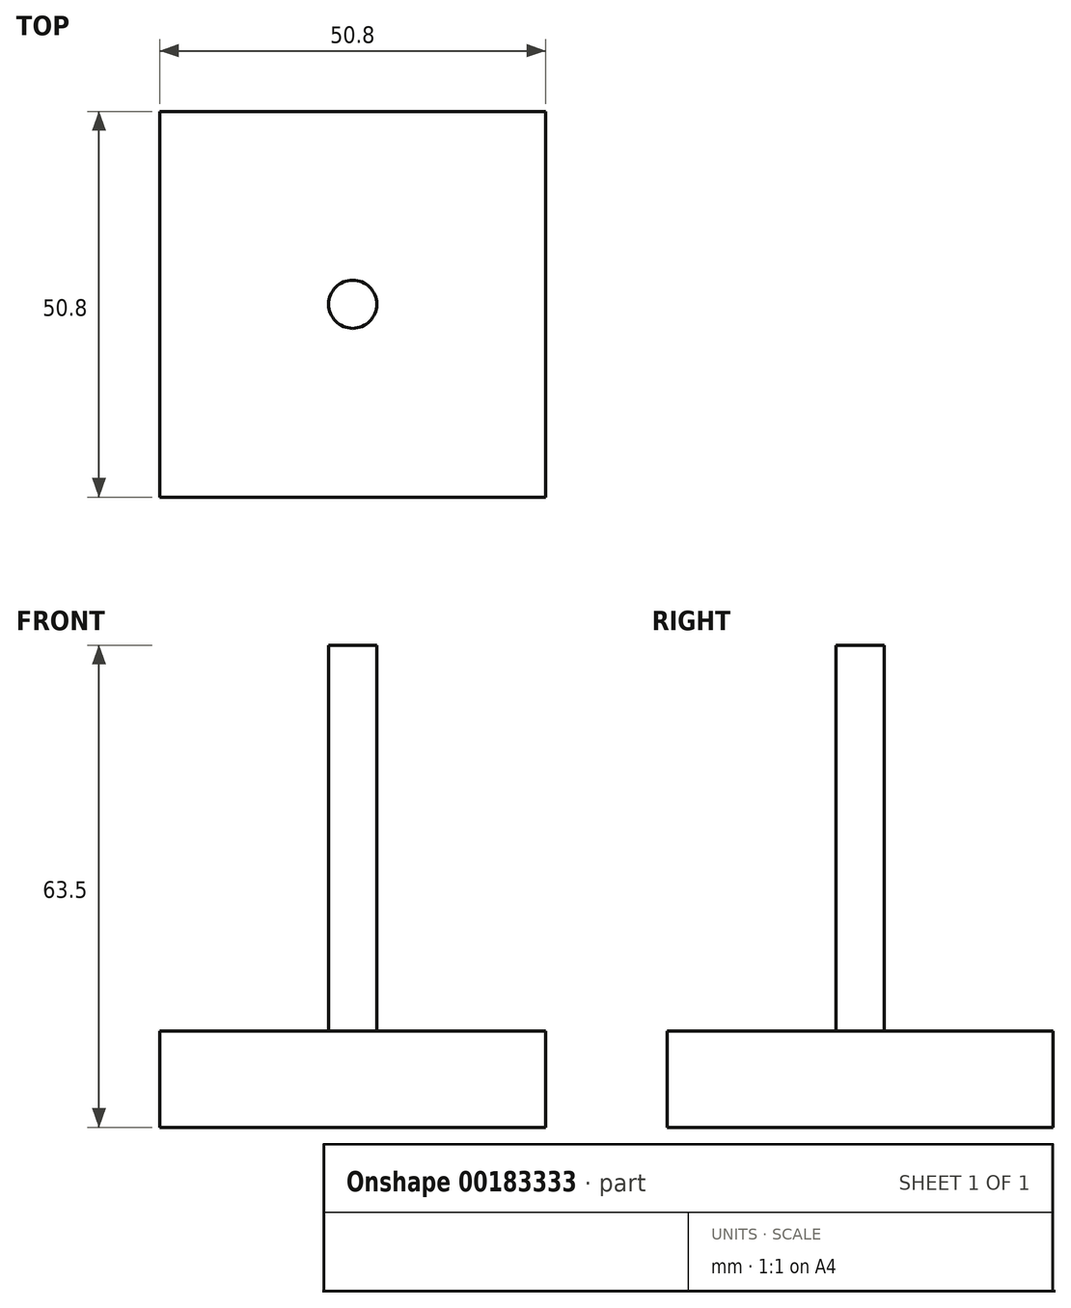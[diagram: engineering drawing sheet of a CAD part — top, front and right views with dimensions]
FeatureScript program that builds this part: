
annotation { "Feature Type Name" : "Feature", "Feature Type Description" : "" }
export const myFeature = defineFeature(function(context is Context, id is Id, definition is map)
    precondition{}
    {
        {
            var Q0;
            Q0=qCreatedBy(makeId("Top.planeOp"),FACE);
            var sketch = newSketch(context, id + "F0", { "sketchPlane" : qUnion([Q0])});
            skLineSegment(sketch, "E0.bottom", {"start": v(25.4, -25.4) * mm, "end": v(-25.4, -25.4) * mm});
            skLineSegment(sketch, "E0.top", {"start": v(25.4, 25.4) * mm, "end": v(-25.4, 25.4) * mm});
            skLineSegment(sketch, "E0.left", {"start": v(25.4, -25.4) * mm, "end": v(25.4, 25.4) * mm});
            skLineSegment(sketch, "E0.right", {"start": v(-25.4, -25.4) * mm, "end": v(-25.4, 25.4) * mm});
            skPoint(sketch, "E0.middle", {"position": v(0, 0) * mm});
            skSolve(sketch);
        }
        {
            var Q0;
            Q0 = qSketchRegion(id + "F0", true);
            extrude(context, id + "F1", {"entities" : qUnion([Q0]), "depth" : 12.7 * mm});
        }
        {
            var Q0;
            Q0=makeQuery(id+"F1.opExtrude","CAP_FACE",FACE,{"disambiguationData":[OSD([sQuery(id+"F0.wireOp",EDGE,"E0.bottom"),sQuery(id+"F0.wireOp",EDGE,"E0.top"),sQuery(id+"F0.wireOp",EDGE,"E0.left"),sQuery(id+"F0.wireOp",EDGE,"E0.right")])],"isStart":false});
            var sketch = newSketch(context, id + "F2", { "sketchPlane" : qUnion([Q0])});
            skCircle(sketch, "E1", {"center": v(0, 0) * mm, "radius": 3.18 * mm});
            skSolve(sketch);
        }
        {
            var Q0;
            Q0 = qSketchRegion(id + "F2", true);
            extrude(context, id + "F3", {"entities" : qUnion([Q0]), "depth" : 50.8 * mm});
        }
    });
